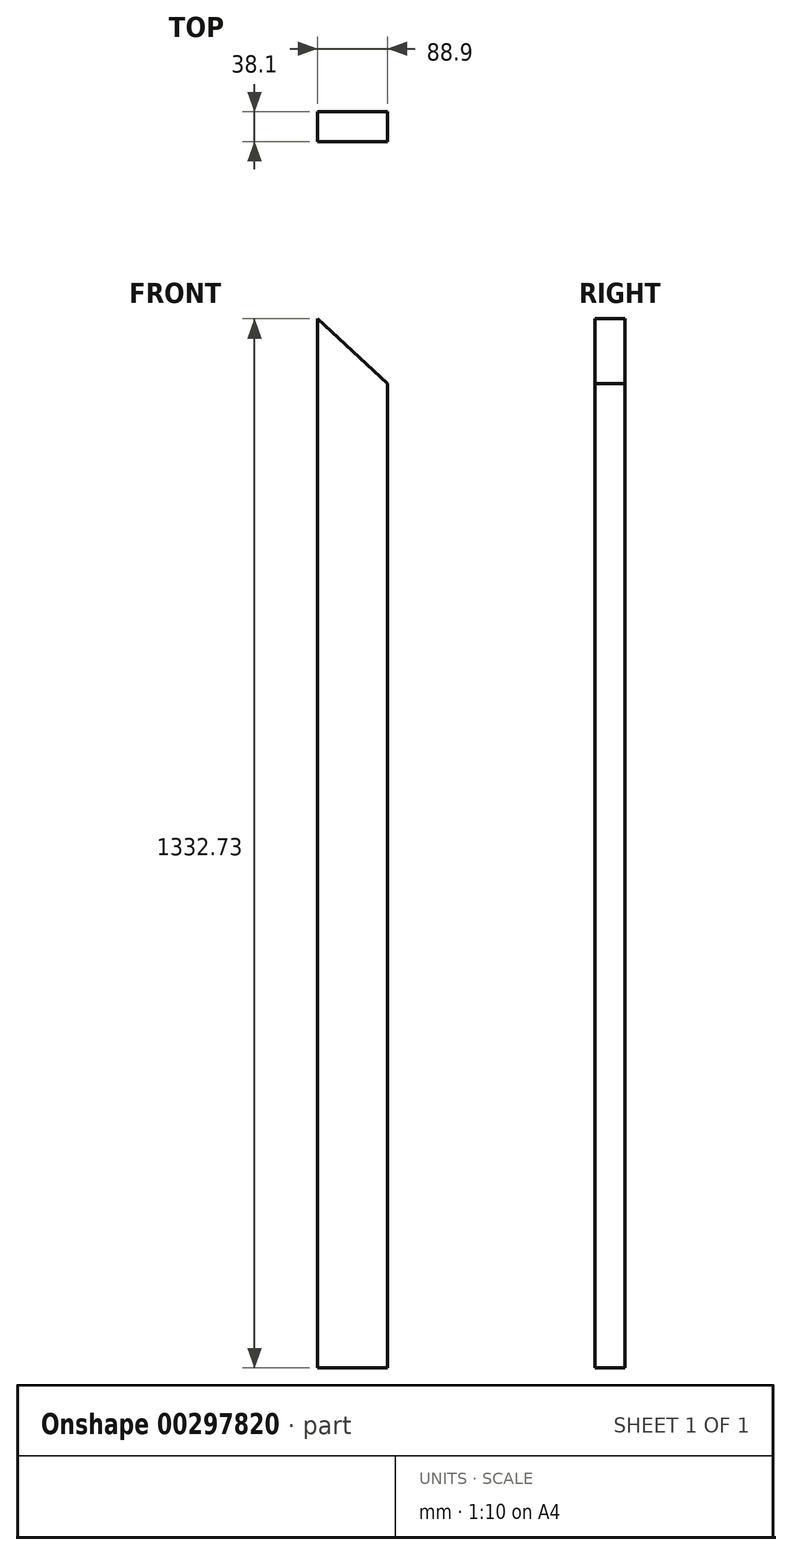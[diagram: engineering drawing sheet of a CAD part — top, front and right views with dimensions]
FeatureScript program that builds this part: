
annotation { "Feature Type Name" : "Feature", "Feature Type Description" : "" }
export const myFeature = defineFeature(function(context is Context, id is Id, definition is map)
    precondition{}
    {
        {
            var Q0;
            Q0=qCreatedBy(makeId("Top.planeOp"),FACE);
            var sketch = newSketch(context, id + "F0", { "sketchPlane" : qUnion([Q0])});
            skLineSegment(sketch, "E0.bottom", {"start": v(0, 0) * mm, "end": v(88.9, 0) * mm});
            skLineSegment(sketch, "E0.top", {"start": v(0, 38.1) * mm, "end": v(88.9, 38.1) * mm});
            skLineSegment(sketch, "E0.left", {"start": v(0, 0) * mm, "end": v(0, 38.1) * mm});
            skLineSegment(sketch, "E0.right", {"start": v(88.9, 0) * mm, "end": v(88.9, 38.1) * mm});
            skSolve(sketch);
        }
        {
            var Q0;
            Q0=makeQuery(id+"F0.imprint","IMPRINT",FACE,{"disambiguationData":[TD([[makeQuery(id+"F0.imprint","IMPRINT",EDGE,{"derivedFrom":sQuery(id+"F0.wireOp",EDGE,"E0.bottom")}),1.0]])]});
            extrude(context, id + "F1", {"entities" : qUnion([Q0]), "depth" : 1371.6 * mm});
        }
        {
            var Q0;
            Q0=makeQuery(id+"F1.opExtrude","SWEPT_FACE",FACE,{"disambiguationData":[OSD([sQuery(id+"F0.wireOp",EDGE,"E0.bottom")])]});
            var sketch = newSketch(context, id + "F2", { "sketchPlane" : qUnion([Q0])});
            skLineSegment(sketch, "E1", {"start": v(88.9, 1371.6) * mm, "end": v(508, 862.83) * mm});
            skLineSegment(sketch, "E2", {"start": v(88.9, 1371.6) * mm, "end": v(28.53, 1306.34) * mm});
            skLineSegment(sketch, "E3", {"start": v(-159.33, 1480.12) * mm, "end": v(508, 862.83) * mm});
            skLineSegment(sketch, "E4", {"start": v(-159.33, 1480.12) * mm, "end": v(88.9, 1480.12) * mm});
            skLineSegment(sketch, "E5", {"start": v(88.9, 1480.12) * mm, "end": v(508, 862.83) * mm});
            skSolve(sketch);
        }
        {
            var Q0;
            {var subQ0=sQuery(id+"F2.wireOp",EDGE,"E2");Q0=makeQuery(id+"F2.imprint","IMPRINT",FACE,{"disambiguationData":[TD([[makeQuery(id+"F2.imprint","IMPRINT",EDGE,{"derivedFrom":subQ0}),-1.0]])]});}
            var Q1;
            {var subQ0=sQuery(id+"F2.wireOp",EDGE,"E2");Q1=makeQuery(id+"F2.imprint","IMPRINT",FACE,{"disambiguationData":[TD([[makeQuery(id+"F2.imprint","IMPRINT",EDGE,{"derivedFrom":subQ0}),1.0]])]});}
            extrude(context, id + "F3", {"entities" : qUnion([Q0, Q1]), "operationType" : NewBodyOperationType.REMOVE, "endBound" : BoundingType.THROUGH_ALL, "oppositeDirection" : true, "depth" : 25.4 * mm});
        }
    });
